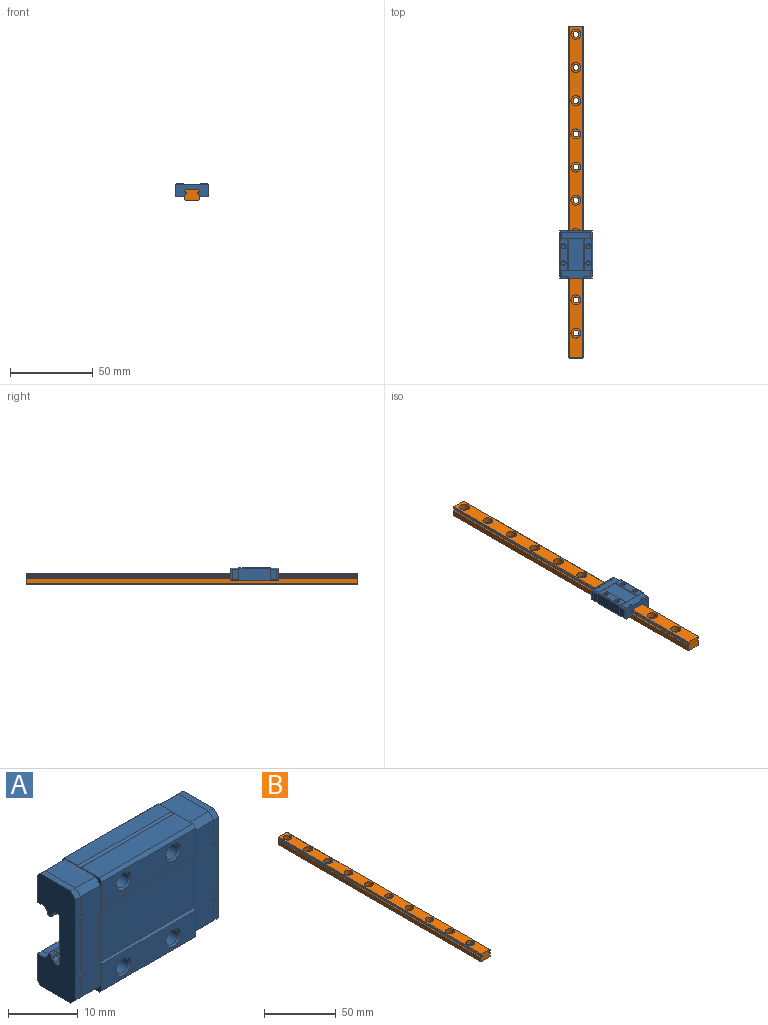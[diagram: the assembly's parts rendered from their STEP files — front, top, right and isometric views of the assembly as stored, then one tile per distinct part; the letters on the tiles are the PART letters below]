
ASSEMBLY  parts=2 mates=1
PART A: 239 faces, bbox 29x8.1x20.1 mm
  f0: plane 0.11x0.01mm, normal (0,0,1), area 0mm2, adj f1,f2,f238
  f1: revolved ~0.04x0.02mm, area 0mm2, adj f0,f2,f238
  f2: plane 17.72x5.12mm, normal (0,-1,0), area 86.8mm2, adj f0,f1,f3,f39,f40,f41,f42,f78
  f3: plane 4x1mm, normal (0,-0.71,0.71), area 5.7mm2, adj f2,f4,f87,f89
  f4: plane 6.1x4mm, normal (0,0,1), area 24.4mm2, adj f3,f5,f87,f89
  f5: plane 4x0.6mm, normal (0,0.71,0.71), area 3.4mm2, adj f4,f6,f87,f89
  f6: plane 4.7x4mm, normal (0,1,0), area 18.8mm2, adj f5,f7,f87,f89
  f7: plane 4x1.41mm, normal (0,0,-1), area 5.6mm2, adj f6,f8,f87,f89
  f8: cylinder r=0.2mm len=4mm, axis (-1,0,0), area 0.9mm2, adj f7,f9,f87,f89
  f9: cylinder r=1mm len=4mm, axis (-1,0,0), area 2.3mm2, adj f8,f10,f87,f89
  f10: cylinder r=0.2mm len=4mm, axis (-1,0,0), area 0.7mm2, adj f9,f11,f87,f89
  f11: plane 4x0.32mm, normal (0,1,-0.09), area 1.3mm2, adj f10,f12,f87,f89
  f12: cylinder r=0.2mm len=4mm, axis (1,0,0), area 1.2mm2, adj f11,f13,f87,f89
  f13: plane 4x0.41mm, normal (0,0,-1), area 1.7mm2, adj f12,f14,f87,f89
  f14: cylinder r=0.2mm len=4mm, axis (-1,0,0), area 1.2mm2, adj f13,f15,f87,f89
  f15: plane 4x0.32mm, normal (0,-1,-0.09), area 1.3mm2, adj f14,f16,f87,f89
  f16: cylinder r=0.2mm len=4mm, axis (-1,0,0), area 0.7mm2, adj f15,f17,f87,f89
  f17: cylinder r=1mm len=4mm, axis (-1,0,0), area 2.3mm2, adj f16,f18,f87,f89
  f18: cylinder r=0.2mm len=4mm, axis (-1,0,0), area 0.9mm2, adj f17,f19,f87,f89
  f19: plane 4x0.51mm, normal (0,0,-1), area 2mm2, adj f18,f20,f87,f89
  f20: plane 4x0.4mm, normal (0,0.71,-0.71), area 2.3mm2, adj f19,f21,f87,f89
  f21: plane 8.2x4mm, normal (0,1,0), area 32.8mm2, adj f20,f22,f87,f89
  f22: plane 4x0.4mm, normal (0,0.71,0.71), area 2.3mm2, adj f21,f23,f87,f89
  f23: plane 4x0.51mm, normal (0,0,1), area 2mm2, adj f22,f24,f87,f89
  f24: cylinder r=0.2mm len=4mm, axis (-1,0,0), area 0.9mm2, adj f23,f25,f87,f89
  f25: cylinder r=1mm len=4mm, axis (-1,0,0), area 2.3mm2, adj f24,f26,f87,f89
  f26: cylinder r=0.2mm len=4mm, axis (-1,0,0), area 0.7mm2, adj f25,f27,f87,f89
  f27: plane 4x0.32mm, normal (0,-1,0.09), area 1.3mm2, adj f26,f28,f87,f89
  f28: cylinder r=0.2mm len=4mm, axis (-1,0,0), area 1.2mm2, adj f27,f29,f87,f89
  f29: plane 4x0.41mm, normal (0,0,1), area 1.7mm2, adj f28,f30,f87,f89
  f30: cylinder r=0.2mm len=4mm, axis (-1,0,0), area 1.2mm2, adj f29,f31,f87,f89
  f31: plane 4x0.32mm, normal (0,1,0.09), area 1.3mm2, adj f30,f32,f87,f89
  f32: cylinder r=0.2mm len=4mm, axis (-1,0,0), area 0.7mm2, adj f31,f33,f87,f89
  f33: cylinder r=1mm len=4mm, axis (-1,0,0), area 2.3mm2, adj f32,f34,f87,f89
  f34: cylinder r=0.2mm len=4mm, axis (-1,0,0), area 0.9mm2, adj f33,f35,f87,f89
  f35: plane 4x1.41mm, normal (0,0,1), area 5.6mm2, adj f34,f36,f87,f89
  f36: plane 4.7x4mm, normal (0,1,0), area 18.8mm2, adj f35,f37,f87,f89
  f37: plane 4x0.6mm, normal (0,0.71,-0.71), area 3.4mm2, adj f36,f38,f87,f89
  f38: plane 6.1x4mm, normal (0,0,-1), area 24.4mm2, adj f37,f87,f88,f89
  f39: plane 0.96x0.1mm, normal (-1,0,0), area 0.1mm2, adj f2,f40,f238
  f40: plane 0.54x0.05mm, normal (0,0,-1), area 0mm2, adj f2,f39,f238
  f41: revolved ~0.7x0.04mm, area 0mm2, adj f2,f238
  f42: plane 1x1mm, normal (0,-0.71,0.71), area 1.4mm2, adj f2,f43,f78,f80
  f43: plane 6.1x1mm, normal (0,0,1), area 6.1mm2, adj f42,f44,f78,f80
  f44: plane 1x0.6mm, normal (0,0.71,0.71), area 0.8mm2, adj f43,f45,f78,f80
  f45: plane 4.7x1mm, normal (0,1,0), area 4.7mm2, adj f44,f46,f78,f80
  f46: plane 1.41x1mm, normal (0,0,-1), area 1.4mm2, adj f45,f47,f78,f80
  f47: cylinder r=0.2mm len=1mm, axis (-1,0,0), area 0.2mm2, adj f46,f48,f78,f80
  f48: cylinder r=1mm len=1mm, axis (-1,0,0), area 0.6mm2, adj f47,f49,f78,f80
  f49: cylinder r=0.2mm len=1mm, axis (-1,0,0), area 0.2mm2, adj f48,f50,f78,f80
  f50: plane 1x0.32mm, normal (0,1,-0.09), area 0.3mm2, adj f49,f51,f78,f80
  f51: cylinder r=0.2mm len=1mm, axis (-1,0,0), area 0.3mm2, adj f50,f52,f78,f80
  f52: plane 1x0.41mm, normal (0,0,-1), area 0.4mm2, adj f51,f53,f78,f80
  f53: cylinder r=0.2mm len=1mm, axis (-1,0,0), area 0.3mm2, adj f52,f54,f78,f80
  f54: plane 1x0.32mm, normal (0,-1,-0.09), area 0.3mm2, adj f53,f55,f78,f80
  f55: cylinder r=0.2mm len=1mm, axis (-1,0,0), area 0.2mm2, adj f54,f56,f78,f80
  f56: cylinder r=1mm len=1mm, axis (-1,0,0), area 0.6mm2, adj f55,f57,f78,f80
  f57: cylinder r=0.2mm len=1mm, axis (-1,0,0), area 0.2mm2, adj f56,f58,f78,f80
  f58: plane 1x0.51mm, normal (0,0,-1), area 0.5mm2, adj f57,f59,f78,f80
  f59: plane 1x0.4mm, normal (0,0.71,-0.71), area 0.6mm2, adj f58,f60,f78,f80
  f60: plane 8.2x1mm, normal (0,1,0), area 8.2mm2, adj f59,f61,f78,f80
  f61: plane 1x0.4mm, normal (0,0.71,0.71), area 0.6mm2, adj f60,f62,f78,f80
  f62: plane 1x0.51mm, normal (0,0,1), area 0.5mm2, adj f61,f63,f78,f80
  f63: cylinder r=0.2mm len=1mm, axis (-1,0,0), area 0.2mm2, adj f62,f64,f78,f80
  f64: cylinder r=1mm len=1mm, axis (-1,0,0), area 0.6mm2, adj f63,f65,f78,f80
  f65: cylinder r=0.2mm len=1mm, axis (-1,0,0), area 0.2mm2, adj f64,f66,f78,f80
  f66: plane 1x0.32mm, normal (0,-1,0.09), area 0.3mm2, adj f65,f67,f78,f80
  f67: cylinder r=0.2mm len=1mm, axis (-1,0,0), area 0.3mm2, adj f66,f68,f78,f80
  f68: plane 1x0.41mm, normal (0,0,1), area 0.4mm2, adj f67,f69,f78,f80
  f69: cylinder r=0.2mm len=1mm, axis (-1,0,0), area 0.3mm2, adj f68,f70,f78,f80
  f70: plane 1x0.32mm, normal (0,1,0.09), area 0.3mm2, adj f69,f71,f78,f80
  f71: cylinder r=0.2mm len=1mm, axis (-1,0,0), area 0.2mm2, adj f70,f72,f78,f80
  f72: cylinder r=1mm len=1mm, axis (-1,0,0), area 0.6mm2, adj f71,f73,f78,f80
  f73: cylinder r=0.2mm len=1mm, axis (-1,0,0), area 0.2mm2, adj f72,f74,f78,f80
  f74: plane 1.41x1mm, normal (0,0,1), area 1.4mm2, adj f73,f75,f78,f80
  f75: plane 4.7x1mm, normal (0,1,0), area 4.7mm2, adj f74,f76,f78,f80
  f76: plane 1x0.6mm, normal (0,0.71,-0.71), area 0.8mm2, adj f75,f77,f78,f80
  f77: plane 6.1x1mm, normal (0,0,-1), area 6.1mm2, adj f76,f78,f79,f80
  f78: plane 19.6x7.7mm, normal (1,0,0), area 112.1mm2, adj f2,f42,f43,f44,f45,f46,f47,f48
  f79: plane 1x1mm, normal (0,-0.71,-0.71), area 1.4mm2, adj f2,f77,f78,f80
  f80: plane 19.6x7.7mm, normal (-1,0,0), area 96.6mm2, adj f2,f42,f43,f44,f45,f46,f47,f48
  f81: revolved ~0.7x0.04mm, area 0mm2, adj f2,f86
  f82: revolved ~0.04x0.02mm, area 0mm2, adj f2,f83,f86
  f83: plane 0.11x0.01mm, normal (0,0,-1), area 0mm2, adj f2,f82,f86
  f84: plane 0.54x0.05mm, normal (0,0,1), area 0mm2, adj f2,f85,f86
  f85: plane 0.96x0.1mm, normal (-1,0,0), area 0.1mm2, adj f2,f84,f86
  f86: cone r=1.57mm half-angle=5deg, axis (-1,0,0), area 0.6mm2, adj f2,f80,f81,f82,f83,f84,f85,f87
  f87: plane 19.6x7.7mm, normal (1,0,0), area 96.6mm2, adj f2,f3,f4,f5,f6,f7,f8,f9
  f88: plane 4x1mm, normal (0,-0.71,-0.71), area 5.7mm2, adj f2,f38,f87,f89
  f89: plane 19.6x7.7mm, normal (-1,0,0), area 108mm2, adj f2,f3,f4,f5,f6,f7,f8,f9
  f90: cylinder r=0.8mm len=1.6mm, axis (-1,0,0), area 0mm2, adj f89,f91
  f91: plane 20x8mm, normal (1,0,0), area 115mm2, adj f90,f92,f182,f183,f184,f185,f186,f187
  f92: cylinder r=0.2mm len=18.9mm, axis (-1,0,0), area 3.5mm2, adj f91,f93,f182,f236
  f93: plane 20x8mm, normal (-1,0,0), area 115mm2, adj f92,f94,f181,f182,f183,f184,f185,f186
  f94: cylinder r=0.8mm len=1.6mm, axis (1,0,0), area 0mm2, adj f93,f95
  f95: plane 19.6x7.7mm, normal (1,0,0), area 108mm2, adj f94,f96,f144,f145,f146,f147,f148,f149
  f96: cylinder r=0.2mm len=4mm, axis (1,0,0), area 0.7mm2, adj f95,f97,f144,f180
  f97: plane 19.6x7.7mm, normal (-1,0,0), area 96.6mm2, adj f96,f98,f142,f144,f145,f146,f147,f148
  f98: cone r=1.6mm half-angle=5deg, axis (1,0,0), area 0.6mm2, adj f97,f99,f100,f140,f141,f167
  f99: revolved ~0.7x0.04mm, area 0mm2, adj f98,f100
  f100: plane 17.72x1.12mm, normal (0,-1,0), area 17mm2, adj f98,f99,f101,f102,f138,f139,f140,f142
  f101: revolved ~0.7x0.04mm, area 0mm2, adj f100,f142
  f102: plane 1x1mm, normal (0,-0.71,-0.71), area 1.4mm2, adj f100,f103,f138,f140
  f103: plane 6.1x1mm, normal (0,0,-1), area 6.1mm2, adj f102,f104,f138,f140
  f104: plane 1x0.6mm, normal (0,0.71,-0.71), area 0.8mm2, adj f103,f105,f138,f140
  f105: plane 4.7x1mm, normal (0,1,0), area 4.7mm2, adj f104,f106,f138,f140
  f106: plane 1.41x1mm, normal (0,0,1), area 1.4mm2, adj f105,f107,f138,f140
  f107: cylinder r=0.2mm len=1mm, axis (1,0,0), area 0.2mm2, adj f106,f108,f138,f140
  f108: cylinder r=1mm len=1mm, axis (1,0,0), area 0.6mm2, adj f107,f109,f138,f140
  f109: cylinder r=0.2mm len=1mm, axis (1,0,0), area 0.2mm2, adj f108,f110,f138,f140
  f110: plane 1x0.32mm, normal (0,1,0.09), area 0.3mm2, adj f109,f111,f138,f140
  f111: cylinder r=0.2mm len=1mm, axis (1,0,0), area 0.3mm2, adj f110,f112,f138,f140
  f112: plane 1x0.41mm, normal (0,0,1), area 0.4mm2, adj f111,f113,f138,f140
  f113: cylinder r=0.2mm len=1mm, axis (1,0,0), area 0.3mm2, adj f112,f114,f138,f140
  f114: plane 1x0.32mm, normal (0,-1,0.09), area 0.3mm2, adj f113,f115,f138,f140
  f115: cylinder r=0.2mm len=1mm, axis (1,0,0), area 0.2mm2, adj f114,f116,f138,f140
  f116: cylinder r=1mm len=1mm, axis (1,0,0), area 0.6mm2, adj f115,f117,f138,f140
  f117: cylinder r=0.2mm len=1mm, axis (1,0,0), area 0.2mm2, adj f116,f118,f138,f140
  f118: plane 1x0.51mm, normal (0,0,1), area 0.5mm2, adj f117,f119,f138,f140
  f119: plane 1x0.4mm, normal (0,0.71,0.71), area 0.6mm2, adj f118,f120,f138,f140
  f120: plane 8.2x1mm, normal (0,1,0), area 8.2mm2, adj f119,f121,f138,f140
  f121: plane 1x0.4mm, normal (0,0.71,-0.71), area 0.6mm2, adj f120,f122,f138,f140
  f122: plane 1x0.51mm, normal (0,0,-1), area 0.5mm2, adj f121,f123,f138,f140
  f123: cylinder r=0.2mm len=1mm, axis (1,0,0), area 0.2mm2, adj f122,f124,f138,f140
  f124: cylinder r=1mm len=1mm, axis (1,0,0), area 0.6mm2, adj f123,f125,f138,f140
  f125: cylinder r=0.2mm len=1mm, axis (1,0,0), area 0.2mm2, adj f124,f126,f138,f140
  f126: plane 1x0.32mm, normal (0,-1,-0.09), area 0.3mm2, adj f125,f127,f138,f140
  f127: cylinder r=0.2mm len=1mm, axis (1,0,0), area 0.3mm2, adj f126,f128,f138,f140
  f128: plane 1x0.41mm, normal (0,0,-1), area 0.4mm2, adj f127,f129,f138,f140
  f129: cylinder r=0.2mm len=1mm, axis (1,0,0), area 0.3mm2, adj f128,f130,f138,f140
  f130: plane 1x0.32mm, normal (0,1,-0.09), area 0.3mm2, adj f129,f131,f138,f140
  f131: cylinder r=0.2mm len=1mm, axis (1,0,0), area 0.2mm2, adj f130,f132,f138,f140
  f132: cylinder r=1mm len=1mm, axis (1,0,0), area 0.6mm2, adj f131,f133,f138,f140
  f133: cylinder r=0.2mm len=1mm, axis (1,0,0), area 0.2mm2, adj f132,f134,f138,f140
  f134: plane 1.41x1mm, normal (0,0,-1), area 1.4mm2, adj f133,f135,f138,f140
  f135: plane 4.7x1mm, normal (0,1,0), area 4.7mm2, adj f134,f136,f138,f140
  f136: plane 1x0.6mm, normal (0,0.71,0.71), area 0.8mm2, adj f135,f137,f138,f140
  f137: plane 6.1x1mm, normal (0,0,1), area 6.1mm2, adj f136,f138,f139,f140
  f138: plane 19.6x7.7mm, normal (-1,0,0), area 112.1mm2, adj f100,f102,f103,f104,f105,f106,f107,f108
  f139: plane 1x1mm, normal (0,-0.71,0.71), area 1.4mm2, adj f100,f137,f138,f140
  f140: plane 19.6x7.7mm, normal (1,0,0), area 96.6mm2, adj f98,f100,f102,f103,f104,f105,f106,f107
  f141: plane 1.11x0.1mm, normal (1,0,0), area 0.1mm2, adj f98,f167
  f142: cone r=1.6mm half-angle=5deg, axis (1,0,0), area 0.6mm2, adj f97,f100,f101,f140,f143,f167
  f143: plane 1.11x0.1mm, normal (1,0,0), area 0.1mm2, adj f142,f167
  f144: cylinder r=1mm len=4mm, axis (1,0,0), area 2.3mm2, adj f95,f96,f97,f145
  f145: cylinder r=0.2mm len=4mm, axis (1,0,0), area 0.9mm2, adj f95,f97,f144,f146
  f146: plane 4x0.51mm, normal (0,0,-1), area 2mm2, adj f95,f97,f145,f147
  f147: plane 4x0.4mm, normal (0,0.71,-0.71), area 2.3mm2, adj f95,f97,f146,f148
  f148: plane 8.2x4mm, normal (0,1,0), area 32.8mm2, adj f95,f97,f147,f149
  f149: plane 4x0.4mm, normal (0,0.71,0.71), area 2.3mm2, adj f95,f97,f148,f150
  f150: plane 4x0.51mm, normal (0,0,1), area 2mm2, adj f95,f97,f149,f151
  f151: cylinder r=0.2mm len=4mm, axis (1,0,0), area 0.9mm2, adj f95,f97,f150,f152
  f152: cylinder r=1mm len=4mm, axis (1,0,0), area 2.3mm2, adj f95,f97,f151,f153
  f153: cylinder r=0.2mm len=4mm, axis (1,0,0), area 0.7mm2, adj f95,f97,f152,f154
  f154: plane 4x0.32mm, normal (0,-1,0.09), area 1.3mm2, adj f95,f97,f153,f155
  f155: cylinder r=0.2mm len=4mm, axis (1,0,0), area 1.2mm2, adj f95,f97,f154,f156
  f156: plane 4x0.41mm, normal (0,0,1), area 1.7mm2, adj f95,f97,f155,f157
  f157: cylinder r=0.2mm len=4mm, axis (1,0,0), area 1.2mm2, adj f95,f97,f156,f158
  f158: plane 4x0.32mm, normal (0,1,0.09), area 1.3mm2, adj f95,f97,f157,f159
  f159: cylinder r=0.2mm len=4mm, axis (1,0,0), area 0.7mm2, adj f95,f97,f158,f160
  f160: cylinder r=1mm len=4mm, axis (1,0,0), area 2.3mm2, adj f95,f97,f159,f161
  f161: cylinder r=0.2mm len=4mm, axis (1,0,0), area 0.9mm2, adj f95,f97,f160,f162
  f162: plane 4x1.41mm, normal (0,0,1), area 5.6mm2, adj f95,f97,f161,f163
  f163: plane 4.7x4mm, normal (0,1,0), area 18.8mm2, adj f95,f97,f162,f164
  f164: plane 4x0.6mm, normal (0,0.71,-0.71), area 3.4mm2, adj f95,f97,f163,f165
  f165: plane 6.1x4mm, normal (0,0,-1), area 24.4mm2, adj f95,f97,f164,f166
  f166: plane 4x1mm, normal (0,-0.71,-0.71), area 5.7mm2, adj f95,f97,f165,f167
  f167: plane 17.6x4mm, normal (0,-1,0), area 69.8mm2, adj f95,f97,f98,f141,f142,f143,f166,f168
  f168: plane 4x1mm, normal (0,-0.71,0.71), area 5.7mm2, adj f95,f97,f167,f169
  f169: plane 6.1x4mm, normal (0,0,1), area 24.4mm2, adj f95,f97,f168,f170
  f170: plane 4x0.6mm, normal (0,0.71,0.71), area 3.4mm2, adj f95,f97,f169,f171
  f171: plane 4.7x4mm, normal (0,1,0), area 18.8mm2, adj f95,f97,f170,f172
  f172: plane 4x1.41mm, normal (0,0,-1), area 5.6mm2, adj f95,f97,f171,f173
  f173: cylinder r=0.2mm len=4mm, axis (1,0,0), area 0.9mm2, adj f95,f97,f172,f174
  f174: cylinder r=1mm len=4mm, axis (1,0,0), area 2.3mm2, adj f95,f97,f173,f175
  f175: cylinder r=0.2mm len=4mm, axis (1,0,0), area 0.7mm2, adj f95,f97,f174,f176
  f176: plane 4x0.32mm, normal (0,1,-0.09), area 1.3mm2, adj f95,f97,f175,f177
  f177: cylinder r=0.2mm len=4mm, axis (1,0,0), area 1.2mm2, adj f95,f97,f176,f178
  f178: plane 4x0.41mm, normal (0,0,-1), area 1.7mm2, adj f95,f97,f177,f179
  f179: cylinder r=0.2mm len=4mm, axis (1,0,0), area 1.2mm2, adj f95,f97,f178,f180
  f180: plane 4x0.32mm, normal (0,-1,-0.09), area 1.3mm2, adj f95,f96,f97,f179
  f181: cylinder r=0.8mm len=1.6mm, axis (1,0,0), area 0mm2, adj f93,f95
  f182: cylinder r=1mm len=18.9mm, axis (-1,0,0), area 11.1mm2, adj f91,f92,f93,f183
  f183: cylinder r=0.2mm len=18.9mm, axis (-1,0,0), area 4.3mm2, adj f91,f93,f182,f184
  f184: plane 18.9x0.51mm, normal (0,0,-1), area 9.6mm2, adj f91,f93,f183,f185
  f185: plane 18.9x0.4mm, normal (0,0.71,-0.71), area 10.7mm2, adj f91,f93,f184,f186
  f186: plane 18.9x8.2mm, normal (0,1,0), area 155mm2, adj f91,f93,f185,f187
  f187: plane 18.9x0.4mm, normal (0,0.71,0.71), area 10.7mm2, adj f91,f93,f186,f188
  f188: plane 18.9x0.51mm, normal (0,0,1), area 9.6mm2, adj f91,f93,f187,f189
  f189: cylinder r=0.2mm len=18.9mm, axis (-1,0,0), area 4.3mm2, adj f91,f93,f188,f190
  f190: cylinder r=1mm len=18.9mm, axis (-1,0,0), area 11.1mm2, adj f91,f93,f189,f191
  f191: cylinder r=0.2mm len=18.9mm, axis (-1,0,0), area 3.5mm2, adj f91,f93,f190,f192
  f192: plane 18.9x0.32mm, normal (0,-1,0.09), area 6mm2, adj f91,f93,f191,f193
  f193: cylinder r=0.2mm len=18.9mm, axis (-1,0,0), area 5.6mm2, adj f91,f93,f192,f194
  f194: plane 18.9x0.41mm, normal (0,0,1), area 7.8mm2, adj f91,f93,f193,f195
  f195: cylinder r=0.2mm len=18.9mm, axis (-1,0,0), area 5.6mm2, adj f91,f93,f194,f196
  f196: plane 18.9x0.32mm, normal (0,1,0.09), area 6mm2, adj f91,f93,f195,f197
  f197: cylinder r=0.2mm len=18.9mm, axis (-1,0,0), area 3.5mm2, adj f91,f93,f196,f198
  f198: cylinder r=1mm len=18.9mm, axis (-1,0,0), area 11.1mm2, adj f91,f93,f197,f199
  f199: cylinder r=0.2mm len=18.9mm, axis (-1,0,0), area 4.3mm2, adj f91,f93,f198,f200
  f200: plane 18.9x1.41mm, normal (0,0,1), area 26.6mm2, adj f91,f93,f199,f201
  f201: plane 18.9x5mm, normal (0,1,0), area 94.5mm2, adj f91,f93,f200,f202
  f202: plane 18.9x0.5mm, normal (0,0.71,-0.71), area 13.4mm2, adj f91,f93,f201,f203
  f203: plane 18.9x7mm, normal (0,0,-1), area 132.3mm2, adj f91,f93,f202,f204
  f204: plane 18.9x0.5mm, normal (0,-0.71,-0.71), area 13.4mm2, adj f91,f93,f203,f205
  f205: plane 18.9x4.6mm, normal (0,-1,0), area 72.8mm2, adj f91,f93,f204,f206,f209,f212
  f206: cone r=1.23mm half-angle=45deg, axis (0,-1,0), area 3.3mm2, adj f205,f207
  f207: cylinder r=1.23mm len=3.48mm, axis (0,-1,0), area 26.9mm2, adj f206,f208
  f208: cone r=1.23mm half-angle=63.4deg, axis (0,-1,0), area 5.3mm2, adj f207
  f209: cone r=1.23mm half-angle=45deg, axis (0,-1,0), area 3.3mm2, adj f205,f210
  f210: cylinder r=1.23mm len=3.48mm, axis (0,-1,0), area 26.9mm2, adj f209,f211
  f211: cone r=1.23mm half-angle=63.4deg, axis (0,-1,0), area 5.3mm2, adj f210
  f212: plane 18.9x0.3mm, normal (0,-0.71,0.71), area 8mm2, adj f91,f93,f205,f213
  f213: plane 18.9x9.2mm, normal (0,-1,0), area 173.9mm2, adj f91,f93,f212,f214
  f214: plane 18.9x0.3mm, normal (0,-0.71,-0.71), area 8mm2, adj f91,f93,f213,f215
  f215: plane 18.9x4.6mm, normal (0,-1,0), area 72.8mm2, adj f91,f93,f214,f216,f219,f222
  f216: cone r=1.23mm half-angle=45deg, axis (0,-1,0), area 3.3mm2, adj f215,f217
  f217: cylinder r=1.23mm len=3.48mm, axis (0,-1,0), area 26.9mm2, adj f216,f218
  f218: cone r=1.23mm half-angle=63.4deg, axis (0,-1,0), area 5.3mm2, adj f217
  f219: cone r=1.23mm half-angle=45deg, axis (0,-1,0), area 3.3mm2, adj f215,f220
  f220: cylinder r=1.23mm len=3.48mm, axis (0,-1,0), area 26.9mm2, adj f219,f221
  f221: cone r=1.23mm half-angle=63.4deg, axis (0,-1,0), area 5.3mm2, adj f220
  f222: plane 18.9x0.5mm, normal (0,-0.71,0.71), area 13.4mm2, adj f91,f93,f215,f223
  f223: plane 18.9x3.65mm, normal (0,0,1), area 69.1mm2, adj f91,f93,f222,f224
  f224: cylinder r=0.4mm len=18.9mm, axis (1,0,0), area 15.8mm2, adj f91,f93,f223,f225
  f225: plane 18.9x2.65mm, normal (0,0,1), area 50.2mm2, adj f91,f93,f224,f226
  f226: plane 18.9x0.5mm, normal (0,0.71,0.71), area 13.4mm2, adj f91,f93,f225,f227
  f227: plane 18.9x5mm, normal (0,1,0), area 94.5mm2, adj f91,f93,f226,f228
  f228: plane 18.9x1.41mm, normal (0,0,-1), area 26.6mm2, adj f91,f93,f227,f229
  f229: cylinder r=0.2mm len=18.9mm, axis (-1,0,0), area 4.3mm2, adj f91,f93,f228,f230
  f230: cylinder r=1mm len=18.9mm, axis (-1,0,0), area 11.1mm2, adj f91,f93,f229,f231
  f231: cylinder r=0.2mm len=18.9mm, axis (-1,0,0), area 3.5mm2, adj f91,f93,f230,f232
  f232: plane 18.9x0.32mm, normal (0,1,-0.09), area 6mm2, adj f91,f93,f231,f233
  f233: cylinder r=0.2mm len=18.9mm, axis (-1,0,0), area 5.6mm2, adj f91,f93,f232,f234
  f234: plane 18.9x0.41mm, normal (0,0,-1), area 7.8mm2, adj f91,f93,f233,f235
  f235: cylinder r=0.2mm len=18.9mm, axis (-1,0,0), area 5.6mm2, adj f91,f93,f234,f236
  f236: plane 18.9x0.32mm, normal (0,-1,-0.09), area 6mm2, adj f91,f92,f93,f235
  f237: cylinder r=0.8mm len=1.6mm, axis (-1,0,0), area 0mm2, adj f89,f91
  f238: cone r=1.57mm half-angle=5deg, axis (-1,0,0), area 0.6mm2, adj f0,f1,f2,f39,f40,f41,f80,f87
PART B: 52 faces, bbox 9x200x6.5 mm
  f0: plane 200x0.8mm, normal (-1,0,0), area 160mm2, adj f1,f19,f20,f21
  f1: plane 200x0.53mm, normal (0,0,1), area 106.7mm2, adj f0,f2,f20,f21
  f2: cylinder r=1mm len=200mm, axis (0,1,0), area 181.3mm2, adj f1,f3,f20,f21
  f3: plane 200x3.18mm, normal (-1,0,0), area 635.6mm2, adj f2,f4,f20,f21
  f4: plane 200x0.35mm, normal (-0.71,0,-0.71), area 100mm2, adj f3,f5,f20,f21
  f5: plane 200x8.29mm, normal (0,0,-1), area 1562.4mm2, adj f4,f6,f20,f21,f22,f25,f28,f31
  f6: plane 200x0.35mm, normal (0.71,0,-0.71), area 100mm2, adj f5,f7,f20,f21
  f7: plane 200x3.18mm, normal (1,0,0), area 635.6mm2, adj f6,f8,f20,f21
  f8: cylinder r=1mm len=200mm, axis (0,1,0), area 181.3mm2, adj f7,f9,f20,f21
  f9: plane 200x0.53mm, normal (0,0,1), area 106.7mm2, adj f8,f10,f20,f21
  f10: plane 200x0.8mm, normal (1,0,0), area 160mm2, adj f9,f11,f20,f21
  f11: plane 200x0.53mm, normal (0,0,-1), area 106.7mm2, adj f10,f12,f20,f21
  f12: cylinder r=1mm len=200mm, axis (0,1,0), area 181.3mm2, adj f11,f13,f20,f21
  f13: plane 200x0.68mm, normal (1,0,0), area 135.6mm2, adj f12,f14,f20,f21
  f14: plane 200x0.35mm, normal (0.71,0,0.71), area 100mm2, adj f13,f15,f20,f21
  f15: plane 200x8.29mm, normal (0,0,1), area 1375.8mm2, adj f14,f16,f20,f21,f24,f27,f30,f33
  f16: plane 200x0.35mm, normal (-0.71,0,0.71), area 100mm2, adj f15,f17,f20,f21
  f17: plane 200x0.68mm, normal (-1,0,0), area 135.6mm2, adj f16,f18,f20,f21
  f18: cylinder r=1mm len=200mm, axis (0,1,0), area 181.3mm2, adj f17,f19,f20,f21
  f19: plane 200x0.53mm, normal (0,0,-1), area 106.7mm2, adj f0,f18,f20,f21
  f20: plane 9x6.5mm, normal (0,-1,0), area 55.3mm2, adj f0,f1,f2,f3,f4,f5,f6,f7
  f21: plane 9x6.5mm, normal (0,1,0), area 55.3mm2, adj f0,f1,f2,f3,f4,f5,f6,f7
  f22: cylinder r=1.75mm len=3.5mm, axis (0,0,1), area 33mm2, adj f5,f23
  f23: plane 6x6mm, normal (0,0,1), area 18.7mm2, adj f22,f24
  f24: cylinder r=3mm len=6mm, axis (0,0,1), area 66mm2, adj f15,f23
  f25: cylinder r=1.75mm len=3.5mm, axis (0,0,1), area 33mm2, adj f5,f26
  f26: plane 6x6mm, normal (0,0,1), area 18.7mm2, adj f25,f27
  f27: cylinder r=3mm len=6mm, axis (0,0,1), area 66mm2, adj f15,f26
  f28: cylinder r=1.75mm len=3.5mm, axis (0,0,1), area 33mm2, adj f5,f29
  f29: plane 6x6mm, normal (0,0,1), area 18.7mm2, adj f28,f30
  f30: cylinder r=3mm len=6mm, axis (0,0,1), area 66mm2, adj f15,f29
  f31: cylinder r=1.75mm len=3.5mm, axis (0,0,1), area 33mm2, adj f5,f32
  f32: plane 6x6mm, normal (0,0,1), area 18.7mm2, adj f31,f33
  f33: cylinder r=3mm len=6mm, axis (0,0,1), area 66mm2, adj f15,f32
  f34: cylinder r=1.75mm len=3.5mm, axis (0,0,1), area 33mm2, adj f5,f35
  f35: plane 6x6mm, normal (0,0,1), area 18.7mm2, adj f34,f36
  f36: cylinder r=3mm len=6mm, axis (0,0,1), area 66mm2, adj f15,f35
  f37: cylinder r=1.75mm len=3.5mm, axis (0,0,1), area 33mm2, adj f5,f38
  f38: plane 6x6mm, normal (0,0,1), area 18.7mm2, adj f37,f39
  f39: cylinder r=3mm len=6mm, axis (0,0,1), area 66mm2, adj f15,f38
  f40: cylinder r=1.75mm len=3.5mm, axis (0,0,1), area 33mm2, adj f5,f41
  f41: plane 6x6mm, normal (0,0,1), area 18.7mm2, adj f40,f42
  f42: cylinder r=3mm len=6mm, axis (0,0,1), area 66mm2, adj f15,f41
  f43: cylinder r=1.75mm len=3.5mm, axis (0,0,1), area 33mm2, adj f5,f44
  f44: plane 6x6mm, normal (0,0,1), area 18.7mm2, adj f43,f45
  f45: cylinder r=3mm len=6mm, axis (0,0,1), area 66mm2, adj f15,f44
  f46: cylinder r=1.75mm len=3.5mm, axis (0,0,1), area 33mm2, adj f5,f47
  f47: plane 6x6mm, normal (0,0,1), area 18.7mm2, adj f46,f48
  f48: cylinder r=3mm len=6mm, axis (0,0,1), area 66mm2, adj f15,f47
  f49: cylinder r=1.75mm len=3.5mm, axis (0,0,1), area 33mm2, adj f5,f50
  f50: plane 6x6mm, normal (0,0,1), area 18.7mm2, adj f49,f51
  f51: cylinder r=3mm len=6mm, axis (0,0,1), area 66mm2, adj f15,f50
PLACE A rot(axis=(-0.58,0.58,-0.58),120deg) t=(0.05,-22.99,2)mm
PLACE B rot(axis=(0,-1,0),0deg) t=(0,100.31,3.25)mm
MATE slider A.f25 <-> B.f2  axis (0,1,0) through (-4.75,-27.99,4.5)mm
